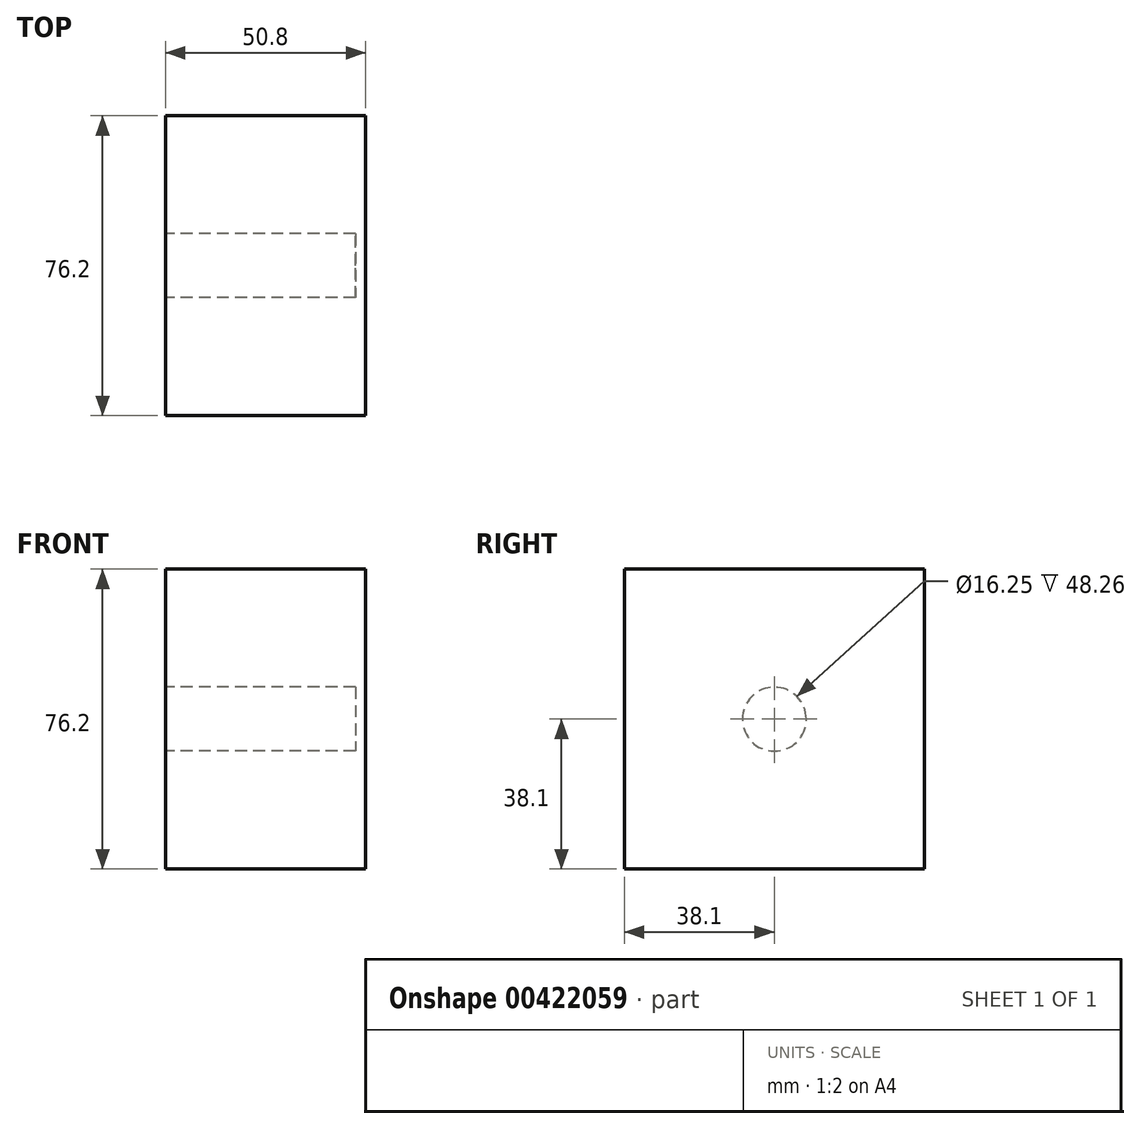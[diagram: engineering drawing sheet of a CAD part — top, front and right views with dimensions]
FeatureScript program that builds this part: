
annotation { "Feature Type Name" : "Feature", "Feature Type Description" : "" }
export const myFeature = defineFeature(function(context is Context, id is Id, definition is map)
    precondition{}
    {
        {
            var Q0;
            Q0=qCreatedBy(makeId("Right.planeOp"),FACE);
            var sketch = newSketch(context, id + "F0", { "sketchPlane" : qUnion([Q0])});
            skLineSegment(sketch, "E0.bottom", {"start": v(38.1, 38.1) * mm, "end": v(-38.1, 38.1) * mm});
            skLineSegment(sketch, "E0.top", {"start": v(38.1, -38.1) * mm, "end": v(-38.1, -38.1) * mm});
            skLineSegment(sketch, "E0.left", {"start": v(38.1, 38.1) * mm, "end": v(38.1, -38.1) * mm});
            skLineSegment(sketch, "E0.right", {"start": v(-38.1, 38.1) * mm, "end": v(-38.1, -38.1) * mm});
            skPoint(sketch, "E0.middle", {"position": v(0, 0) * mm});
            skSolve(sketch);
        }
        {
            var Q0;
            Q0=makeQuery(id+"F0.imprint","IMPRINT",FACE,{"disambiguationData":[TD([[makeQuery(id+"F0.imprint","IMPRINT",EDGE,{"derivedFrom":sQuery(id+"F0.wireOp",EDGE,"E0.bottom")}),1.0]])]});
            extrude(context, id + "F1", {"entities" : qUnion([Q0]), "depth" : 50.8 * mm});
        }
        {
            var Q0;
            Q0=makeQuery(id+"F1.opExtrude","CAP_FACE",FACE,{"disambiguationData":[OSD([sQuery(id+"F0.wireOp",EDGE,"E0.bottom"),sQuery(id+"F0.wireOp",EDGE,"E0.top"),sQuery(id+"F0.wireOp",EDGE,"E0.left"),sQuery(id+"F0.wireOp",EDGE,"E0.right")])],"isStart":true});
            var sketch = newSketch(context, id + "F2", { "sketchPlane" : qUnion([Q0])});
            skCircle(sketch, "E1", {"center": v(0, 0) * mm, "radius": 8.13 * mm});
            skSolve(sketch);
        }
        {
            var Q0;
            Q0=makeQuery(id+"F2.imprint","IMPRINT",FACE,{"disambiguationData":[TD([[makeQuery(id+"F2.imprint","IMPRINT",EDGE,{"derivedFrom":sQuery(id+"F2.wireOp",EDGE,"E1")}),1.0]])]});
            extrude(context, id + "F3", {"entities" : qUnion([Q0]), "operationType" : NewBodyOperationType.REMOVE, "oppositeDirection" : true, "depth" : 48.26 * mm});
        }
    });
